# Revit family: B-4998 Barra de Sujeción para montar en muro
name_source: partatom
category: Plumbing Fixtures
revit_build: Autodesk Revit 2015 (Build: 20140322_1515(x64)
units: mm (PartAtom-declared; Revit-internal decimal feet)

## types (1)
- B-4998 Barra de Sujeción para montar en muro
    Assembly Code = D2010.60
    BT_Color = Cromo
    BT_Itemizado_Estandar_CDT = H 06 06 00
    BT_Material = Cromo
    BT_SKU = 00 00 00
    BT_Uso = Seguridad baño
    Depth = 807 mm
    Description = Barra de Sujeción de acero inoxidable 304, calibre 18 (1,2 mm), acabado satinado y diámetro exterior de 32 mm (1–1/4").
Placa posterior de acero inoxidable, espesor de 5 mm (3/16") y equipada con orificios para su instalación. La barra de sujeción
se levanta manualmente para la aproximación o salida y se baja a la posición horizontal como apoyo. El diseño de contrapeso
impide que la barra de soporte se caiga hacia la posición horizontal una vez que se coloca completamente en posición vertical.
Cumple con las Normas Estándares de Accesibilidad ICC / ANSI A117.1-2003 en EE.UU. Servicio al cliente y manual de piezas
son proporcionados por el fabricante por solicitud.
    Height = 890 mm
    ID_Objeto = BT_F_F_1834
    ID_Source = BIMTOOL
    Keynote = 22 43 39
    Manufacturer = Bobrick
    Model = B-4998 Barra de Sujeción para montar en muro
    Supplier = Mk
    Type Comments = Barra de Sujeción de acero inoxidable 304, calibre 18 (1,2 mm), acabado satinado y diámetro exterior de 32 mm (1–1/4").
Placa posterior de acero inoxidable, espesor de 5 mm (3/16") y equipada con orificios para su instalación. La barra de sujeción
se levanta manualmente para la aproximación o salida y se baja a la posición horizontal como apoyo. El diseño de contrapeso
impide que la barra de soporte se caiga hacia la posición horizontal una vez que se coloca completamente en posición vertical.
Cumple con las Normas Estándares de Accesibilidad ICC / ANSI A117.1-2003 en EE.UU. Servicio al cliente y manual de piezas
son proporcionados por el fabricante por solicitud.
    URL = www.mk.cl
    Width = 155 mm

## geometry (parser evidence)
native form markers: Blend x6, Extrusion x2, Sweep x4
no freeform markers — native parametric forms only
